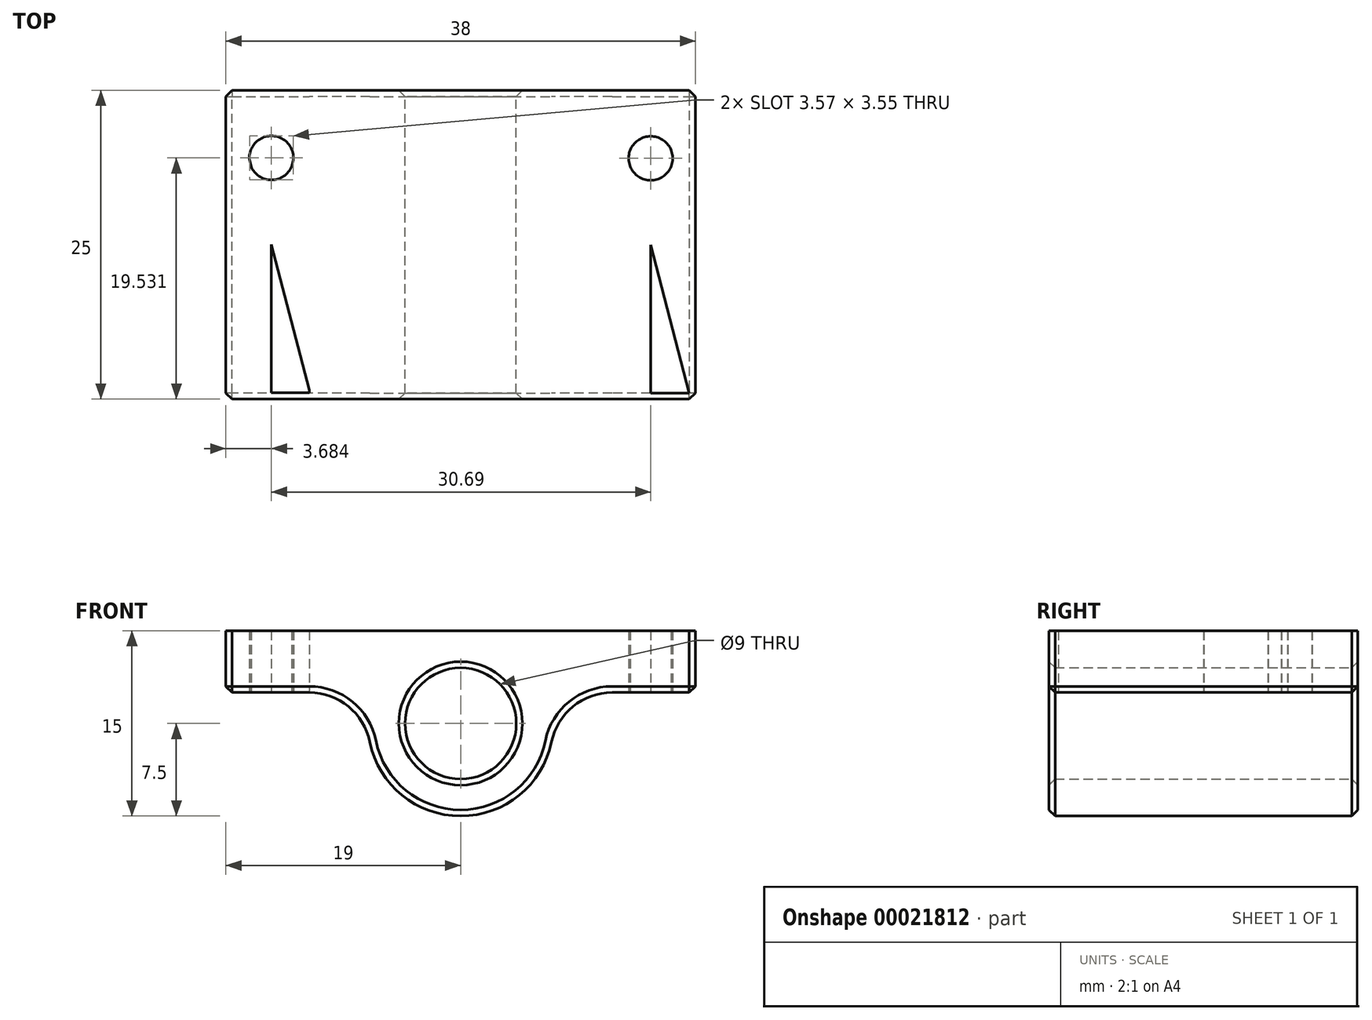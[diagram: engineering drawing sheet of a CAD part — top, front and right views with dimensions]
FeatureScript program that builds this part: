
annotation { "Feature Type Name" : "Feature", "Feature Type Description" : "" }
export const myFeature = defineFeature(function(context is Context, id is Id, definition is map)
    precondition{}
    {
        {
            var Q0;
            Q0=qCreatedBy(makeId("Front.planeOp"),FACE);
            var sketch = newSketch(context, id + "F0", { "sketchPlane" : qUnion([Q0])});
            skCircle(sketch, "E0", {"center": v(0, 0) * mm, "radius": 4.5 * mm});
            skArc(sketch, "E1.0", {"start": v(-7.35, -1.5) * mm, "mid": v(0, -7.5) * mm, "end": v(7.35, -1.5) * mm});
            skLineSegment(sketch, "E2", {"start": v(0, 7.5) * mm, "end": v(-19, 7.5) * mm});
            skLineSegment(sketch, "E3", {"start": v(0, 7.5) * mm, "end": v(19, 7.5) * mm});
            skLineSegment(sketch, "E4.0", {"start": v(12.25, 2.5) * mm, "end": v(19, 2.5) * mm});
            skLineSegment(sketch, "E5.0", {"start": v(-12.25, 2.5) * mm, "end": v(-19, 2.5) * mm});
            skLineSegment(sketch, "E6.0", {"start": v(19, 2.5) * mm, "end": v(19, 7.5) * mm});
            skLineSegment(sketch, "E7.0", {"start": v(-19, 2.5) * mm, "end": v(-19, 7.5) * mm});
            skPoint(sketch, "E8.visualSharp", {"position": v(-7.07, 2.5) * mm});
            skArc(sketch, "E8.filletArc", {"start": v(-7.35, -1.5) * mm, "mid": v(-9.09, 1.37) * mm, "end": v(-12.25, 2.5) * mm});
            skPoint(sketch, "E9.visualSharp", {"position": v(7.07, 2.5) * mm});
            skArc(sketch, "E9.filletArc", {"start": v(12.25, 2.5) * mm, "mid": v(9.09, 1.37) * mm, "end": v(7.35, -1.5) * mm});
            skSolve(sketch);
        }
        {
            var Q0;
            Q0 = qSketchRegion(id + "F0", true);
            extrude(context, id + "F1", {"entities" : qUnion([Q0]), "depth" : 25 * mm});
        }
        {
            var Q0;
            Q0=makeQuery(id+"F1.opExtrude","CAP_EDGE",EDGE,{"disambiguationData":[OSD([sQuery(id+"F0.wireOp",EDGE,"E7.0")])],"isStart":false});
            var Q1;
            Q1=makeQuery(id+"F1.opExtrude","CAP_EDGE",EDGE,{"disambiguationData":[OSD([sQuery(id+"F0.wireOp",EDGE,"E5.0")])],"isStart":false});
            var Q2;
            Q2=makeQuery(id+"F1.opExtrude","CAP_EDGE",EDGE,{"disambiguationData":[OSD([sQuery(id+"F0.wireOp",EDGE,"E6.0")])],"isStart":false});
            var Q3;
            Q3=makeQuery(id+"F1.opExtrude","CAP_EDGE",EDGE,{"disambiguationData":[OSD([sQuery(id+"F0.wireOp",EDGE,"E0")])],"isStart":false});
            var Q4;
            Q4=makeQuery(id+"F1.opExtrude","CAP_EDGE",EDGE,{"disambiguationData":[OSD([sQuery(id+"F0.wireOp",EDGE,"E7.0")])],"isStart":true});
            var Q5;
            Q5=makeQuery(id+"F1.opExtrude","CAP_EDGE",EDGE,{"disambiguationData":[OSD([sQuery(id+"F0.wireOp",EDGE,"E5.0")])],"isStart":true});
            var Q6;
            Q6=makeQuery(id+"F1.opExtrude","CAP_EDGE",EDGE,{"disambiguationData":[OSD([sQuery(id+"F0.wireOp",EDGE,"E8.filletArc")])],"isStart":true});
            var Q7;
            Q7=makeQuery(id+"F1.opExtrude","CAP_EDGE",EDGE,{"disambiguationData":[OSD([sQuery(id+"F0.wireOp",EDGE,"E6.0")])],"isStart":true});
            var Q8;
            Q8=makeQuery(id+"F1.opExtrude","SWEPT_EDGE",EDGE,{"disambiguationData":[OSD([sQuery(id+"F0.wireOp",EDGE,"E4.0"),sQuery(id+"F0.wireOp",EDGE,"E6.0")])]});
            var Q9;
            Q9=makeQuery(id+"F1.opExtrude","SWEPT_EDGE",EDGE,{"disambiguationData":[OSD([sQuery(id+"F0.wireOp",EDGE,"E5.0"),sQuery(id+"F0.wireOp",EDGE,"E7.0")])]});
            var Q10;
            Q10=makeQuery(id+"F1.opExtrude","CAP_EDGE",EDGE,{"disambiguationData":[OSD([sQuery(id+"F0.wireOp",EDGE,"E0")])],"isStart":true});
            chamfer(context, id + "F2", {"entities" : qUnion([Q0, Q1, Q2, Q3, Q4, Q5, Q6, Q7, Q8, Q9, Q10]), "width" : .5 * mm, "tangentPropagation" : true});
        }
        {
            var Q0;
            Q0=makeQuery(id+"F1.opExtrude","SWEPT_FACE",FACE,{"disambiguationData":[OSD([sQuery(id+"F0.wireOp",EDGE,"E4.0")])]});
            var sketch = newSketch(context, id + "F3", { "sketchPlane" : qUnion([Q0])});
            skLineSegment(sketch, "E10", {"start": v(12.25, 24.5) * mm, "end": v(18.5, 0.5) * mm});
            skLineSegment(sketch, "E11", {"start": v(18.5, 24.5) * mm, "end": v(12.25, 0.5) * mm});
            skLineSegment(sketch, "E12", {"start": v(12.25, 24.5) * mm, "end": v(18.5, 24.5) * mm});
            skLineSegment(sketch, "E13", {"start": v(18.5, 0.5) * mm, "end": v(12.25, 0.5) * mm});
            skLineSegment(sketch, "E14.0", {"start": v(12.25, 19.5) * mm, "end": v(18.5, 19.5) * mm});
            skLineSegment(sketch, "E15.0", {"start": v(18.5, 5.5) * mm, "end": v(12.25, 5.5) * mm});
            skLineSegment(sketch, "E16", {"start": v(15.37, 24.5) * mm, "end": v(15.37, 0.5) * mm});
            skCircle(sketch, "E17", {"center": v(15.37, 19.5) * mm, "radius": 1.72 * mm});
            skCircle(sketch, "E18", {"center": v(15.37, 5.5) * mm, "radius": 1.78 * mm});
            skSolve(sketch);
        }
        {
            var Q0;
            {var subQ1=sQuery(id+"F3.wireOp",EDGE,"E16");var subQ3=sQuery(id+"F3.wireOp",EDGE,"E14.0");var subQ5=makeQuery(id+"F3.imprint","INTERSECT",VERTEX,{"derivedFrom":[subQ3,subQ1]});Q0=makeQuery(id+"F3.imprint","IMPRINT",FACE,{"disambiguationData":[TD([[makeQuery(id+"F3.imprint","IMPRINT",EDGE,{"disambiguationData":[TD([[subQ5,-1.0]])],"derivedFrom":subQ3}),1.0]])]});}
            var Q1;
            {var subQ1=sQuery(id+"F3.wireOp",EDGE,"E16");var subQ3=sQuery(id+"F3.wireOp",EDGE,"E14.0");var subQ5=makeQuery(id+"F3.imprint","INTERSECT",VERTEX,{"derivedFrom":[subQ3,subQ1]});Q1=makeQuery(id+"F3.imprint","IMPRINT",FACE,{"disambiguationData":[TD([[makeQuery(id+"F3.imprint","IMPRINT",EDGE,{"disambiguationData":[TD([[subQ5,-1.0]])],"derivedFrom":subQ3}),-1.0]])]});}
            var Q2;
            {var subQ0=sQuery(id+"F3.wireOp",EDGE,"E17");var subQ3=sQuery(id+"F3.wireOp",EDGE,"E14.0");var subQ4=makeQuery(id+"F3.imprint","INTERSECT",VERTEX,{"disambiguationData":[OD(0.0)],"derivedFrom":[subQ3,subQ0]});Q2=makeQuery(id+"F3.imprint","IMPRINT",FACE,{"disambiguationData":[TD([[makeQuery(id+"F3.imprint","IMPRINT",EDGE,{"disambiguationData":[TD([[subQ4,-1.0]])],"derivedFrom":subQ3}),1.0]])]});}
            var Q3;
            {var subQ0=sQuery(id+"F3.wireOp",EDGE,"E17");var subQ3=sQuery(id+"F3.wireOp",EDGE,"E14.0");var subQ4=makeQuery(id+"F3.imprint","INTERSECT",VERTEX,{"disambiguationData":[OD(0.0)],"derivedFrom":[subQ3,subQ0]});Q3=makeQuery(id+"F3.imprint","IMPRINT",FACE,{"disambiguationData":[TD([[makeQuery(id+"F3.imprint","IMPRINT",EDGE,{"disambiguationData":[TD([[subQ4,-1.0]])],"derivedFrom":subQ3}),-1.0]])]});}
            var Q4;
            {var subQ0=sQuery(id+"F3.wireOp",EDGE,"E18");var subQ3=sQuery(id+"F3.wireOp",EDGE,"E10");var subQ8=makeQuery(id+"F3.imprint","INTERSECT",VERTEX,{"disambiguationData":[OD(0.0)],"derivedFrom":[subQ3,subQ0]});Q4=makeQuery(id+"F3.imprint","IMPRINT",FACE,{"disambiguationData":[TD([[makeQuery(id+"F3.imprint","IMPRINT",EDGE,{"disambiguationData":[TD([[subQ8,-1.0]])],"derivedFrom":subQ3}),-1.0]])]});}
            var Q5;
            {var subQ0=sQuery(id+"F3.wireOp",EDGE,"E18");var subQ3=sQuery(id+"F3.wireOp",EDGE,"E11");var subQ8=makeQuery(id+"F3.imprint","INTERSECT",VERTEX,{"disambiguationData":[OD(0.0)],"derivedFrom":[subQ3,subQ0]});Q5=makeQuery(id+"F3.imprint","IMPRINT",FACE,{"disambiguationData":[TD([[makeQuery(id+"F3.imprint","IMPRINT",EDGE,{"disambiguationData":[TD([[subQ8,-1.0]])],"derivedFrom":subQ3}),1.0]])]});}
            var Q6;
            {var subQ1=sQuery(id+"F3.wireOp",EDGE,"E16");var subQ3=sQuery(id+"F3.wireOp",EDGE,"E15.0");var subQ5=makeQuery(id+"F3.imprint","INTERSECT",VERTEX,{"derivedFrom":[subQ3,subQ1]});Q6=makeQuery(id+"F3.imprint","IMPRINT",FACE,{"disambiguationData":[TD([[makeQuery(id+"F3.imprint","IMPRINT",EDGE,{"disambiguationData":[TD([[subQ5,-1.0]])],"derivedFrom":subQ3}),1.0]])]});}
            var Q7;
            {var subQ0=sQuery(id+"F3.wireOp",EDGE,"E18");var subQ3=sQuery(id+"F3.wireOp",EDGE,"E15.0");var subQ4=makeQuery(id+"F3.imprint","INTERSECT",VERTEX,{"disambiguationData":[OD(0.0)],"derivedFrom":[subQ3,subQ0]});Q7=makeQuery(id+"F3.imprint","IMPRINT",FACE,{"disambiguationData":[TD([[makeQuery(id+"F3.imprint","IMPRINT",EDGE,{"disambiguationData":[TD([[subQ4,-1.0]])],"derivedFrom":subQ3}),1.0]])]});}
            extrude(context, id + "F4", {"entities" : qUnion([Q0, Q1, Q2, Q3, Q4, Q5, Q6, Q7]), "operationType" : NewBodyOperationType.REMOVE, "endBound" : BoundingType.THROUGH_ALL, "oppositeDirection" : true, "depth" : 25 * mm});
        }
        {
            var Q0;
            Q0=makeQuery(id+"F1.opExtrude","SWEPT_FACE",FACE,{"disambiguationData":[OSD([sQuery(id+"F0.wireOp",EDGE,"E5.0")])]});
            var sketch = newSketch(context, id + "F5", { "sketchPlane" : qUnion([Q0])});
            skLineSegment(sketch, "E19", {"start": v(-18.44, 24.47) * mm, "end": v(-12.19, 0.47) * mm});
            skLineSegment(sketch, "E20", {"start": v(-12.19, 24.47) * mm, "end": v(-18.44, 0.47) * mm});
            skLineSegment(sketch, "E21", {"start": v(-18.44, 24.47) * mm, "end": v(-12.19, 24.47) * mm});
            skLineSegment(sketch, "E22", {"start": v(-12.19, 0.47) * mm, "end": v(-18.44, 0.47) * mm});
            skLineSegment(sketch, "E23.0", {"start": v(-18.44, 19.47) * mm, "end": v(-12.19, 19.47) * mm});
            skLineSegment(sketch, "E24.0", {"start": v(-12.19, 5.47) * mm, "end": v(-18.44, 5.47) * mm});
            skLineSegment(sketch, "E25", {"start": v(-15.32, 24.47) * mm, "end": v(-15.32, 0.47) * mm});
            skCircle(sketch, "E26", {"center": v(-15.32, 19.47) * mm, "radius": 1.72 * mm});
            skCircle(sketch, "E27", {"center": v(-15.32, 5.47) * mm, "radius": 1.78 * mm});
            skSolve(sketch);
        }
        {
            var Q0;
            {var subQ1=sQuery(id+"F5.wireOp",EDGE,"E25");var subQ3=sQuery(id+"F5.wireOp",EDGE,"E23.0");var subQ5=makeQuery(id+"F5.imprint","INTERSECT",VERTEX,{"derivedFrom":[subQ3,subQ1]});Q0=makeQuery(id+"F5.imprint","IMPRINT",FACE,{"disambiguationData":[TD([[makeQuery(id+"F5.imprint","IMPRINT",EDGE,{"disambiguationData":[TD([[subQ5,-1.0]])],"derivedFrom":subQ3}),1.0]])]});}
            var Q1;
            {var subQ0=sQuery(id+"F5.wireOp",EDGE,"E26");var subQ3=sQuery(id+"F5.wireOp",EDGE,"E23.0");var subQ4=makeQuery(id+"F5.imprint","INTERSECT",VERTEX,{"disambiguationData":[OD(0.0)],"derivedFrom":[subQ3,subQ0]});Q1=makeQuery(id+"F5.imprint","IMPRINT",FACE,{"disambiguationData":[TD([[makeQuery(id+"F5.imprint","IMPRINT",EDGE,{"disambiguationData":[TD([[subQ4,-1.0]])],"derivedFrom":subQ3}),1.0]])]});}
            var Q2;
            {var subQ0=sQuery(id+"F5.wireOp",EDGE,"E26");var subQ3=sQuery(id+"F5.wireOp",EDGE,"E23.0");var subQ4=makeQuery(id+"F5.imprint","INTERSECT",VERTEX,{"disambiguationData":[OD(0.0)],"derivedFrom":[subQ3,subQ0]});Q2=makeQuery(id+"F5.imprint","IMPRINT",FACE,{"disambiguationData":[TD([[makeQuery(id+"F5.imprint","IMPRINT",EDGE,{"disambiguationData":[TD([[subQ4,-1.0]])],"derivedFrom":subQ3}),-1.0]])]});}
            var Q3;
            {var subQ1=sQuery(id+"F5.wireOp",EDGE,"E25");var subQ3=sQuery(id+"F5.wireOp",EDGE,"E23.0");var subQ5=makeQuery(id+"F5.imprint","INTERSECT",VERTEX,{"derivedFrom":[subQ3,subQ1]});Q3=makeQuery(id+"F5.imprint","IMPRINT",FACE,{"disambiguationData":[TD([[makeQuery(id+"F5.imprint","IMPRINT",EDGE,{"disambiguationData":[TD([[subQ5,-1.0]])],"derivedFrom":subQ3}),-1.0]])]});}
            var Q4;
            {var subQ0=sQuery(id+"F5.wireOp",EDGE,"E27");var subQ3=sQuery(id+"F5.wireOp",EDGE,"E19");var subQ4=makeQuery(id+"F5.imprint","INTERSECT",VERTEX,{"disambiguationData":[OD(0.0)],"derivedFrom":[subQ3,subQ0]});Q4=makeQuery(id+"F5.imprint","IMPRINT",FACE,{"disambiguationData":[TD([[makeQuery(id+"F5.imprint","IMPRINT",EDGE,{"disambiguationData":[TD([[subQ4,-1.0]])],"derivedFrom":subQ3}),-1.0]])]});}
            var Q5;
            {var subQ0=sQuery(id+"F5.wireOp",EDGE,"E27");var subQ3=sQuery(id+"F5.wireOp",EDGE,"E20");var subQ8=makeQuery(id+"F5.imprint","INTERSECT",VERTEX,{"disambiguationData":[OD(0.0)],"derivedFrom":[subQ3,subQ0]});Q5=makeQuery(id+"F5.imprint","IMPRINT",FACE,{"disambiguationData":[TD([[makeQuery(id+"F5.imprint","IMPRINT",EDGE,{"disambiguationData":[TD([[subQ8,-1.0]])],"derivedFrom":subQ3}),1.0]])]});}
            var Q6;
            {var subQ1=sQuery(id+"F5.wireOp",EDGE,"E25");var subQ3=sQuery(id+"F5.wireOp",EDGE,"E24.0");var subQ5=makeQuery(id+"F5.imprint","INTERSECT",VERTEX,{"derivedFrom":[subQ3,subQ1]});Q6=makeQuery(id+"F5.imprint","IMPRINT",FACE,{"disambiguationData":[TD([[makeQuery(id+"F5.imprint","IMPRINT",EDGE,{"disambiguationData":[TD([[subQ5,-1.0]])],"derivedFrom":subQ3}),1.0]])]});}
            var Q7;
            {var subQ0=sQuery(id+"F5.wireOp",EDGE,"E27");var subQ3=sQuery(id+"F5.wireOp",EDGE,"E24.0");var subQ4=makeQuery(id+"F5.imprint","INTERSECT",VERTEX,{"disambiguationData":[OD(0.0)],"derivedFrom":[subQ3,subQ0]});Q7=makeQuery(id+"F5.imprint","IMPRINT",FACE,{"disambiguationData":[TD([[makeQuery(id+"F5.imprint","IMPRINT",EDGE,{"disambiguationData":[TD([[subQ4,-1.0]])],"derivedFrom":subQ3}),1.0]])]});}
            extrude(context, id + "F6", {"entities" : qUnion([Q0, Q1, Q2, Q3, Q4, Q5, Q6, Q7]), "operationType" : NewBodyOperationType.REMOVE, "endBound" : BoundingType.THROUGH_ALL, "oppositeDirection" : true, "depth" : 25 * mm});
        }
    });
